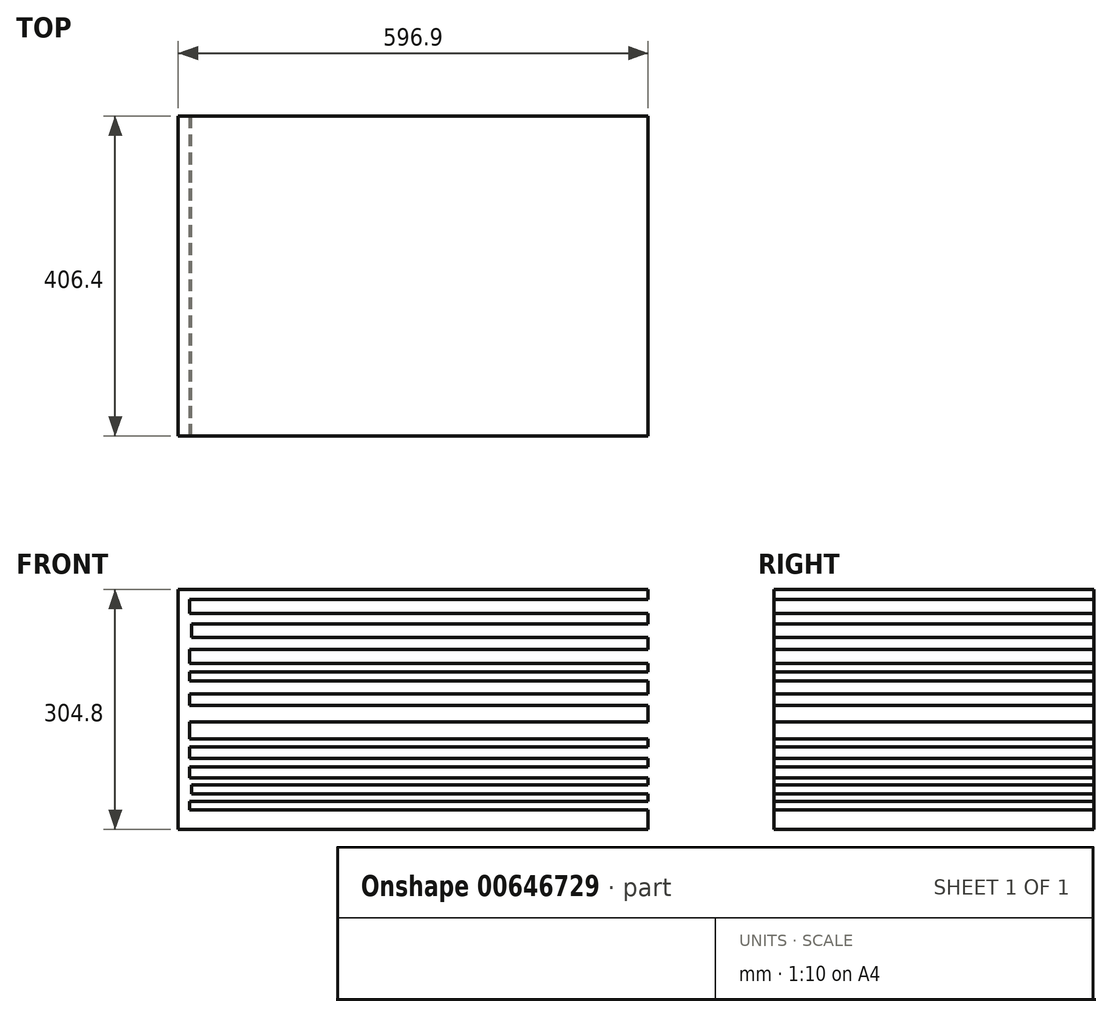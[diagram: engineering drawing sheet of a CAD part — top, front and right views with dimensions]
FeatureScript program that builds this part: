
annotation { "Feature Type Name" : "Feature", "Feature Type Description" : "" }
export const myFeature = defineFeature(function(context is Context, id is Id, definition is map)
    precondition{}
    {
        {
            var Q0;
            Q0=qCreatedBy(makeId("Front.planeOp"),FACE);
            var sketch = newSketch(context, id + "F0", { "sketchPlane" : qUnion([Q0])});
            skLineSegment(sketch, "E0.bottom", {"start": v(-41.59, 248.25) * mm, "end": v(555.31, 248.25) * mm});
            skLineSegment(sketch, "E0.top", {"start": v(-41.59, -56.55) * mm, "end": v(555.31, -56.55) * mm});
            skLineSegment(sketch, "E0.left", {"start": v(-41.59, 248.25) * mm, "end": v(-41.59, -56.55) * mm});
            skLineSegment(sketch, "E0.right", {"start": v(555.31, 248.25) * mm, "end": v(555.31, -56.55) * mm});
            skLineSegment(sketch, "E1.bottom", {"start": v(-26.88, 235.82) * mm, "end": v(557.3, 235.82) * mm});
            skLineSegment(sketch, "E1.top", {"start": v(-26.88, 217.95) * mm, "end": v(557.3, 217.95) * mm});
            skLineSegment(sketch, "E1.left", {"start": v(-26.88, 235.82) * mm, "end": v(-26.88, 217.95) * mm});
            skLineSegment(sketch, "E1.right", {"start": v(557.3, 235.82) * mm, "end": v(557.3, 217.95) * mm});
            skLineSegment(sketch, "E2.bottom", {"start": v(-24.73, 204.36) * mm, "end": v(557.3, 204.36) * mm});
            skLineSegment(sketch, "E2.top", {"start": v(-24.73, 187.2) * mm, "end": v(557.3, 187.2) * mm});
            skLineSegment(sketch, "E2.left", {"start": v(-24.73, 204.36) * mm, "end": v(-24.73, 187.2) * mm});
            skLineSegment(sketch, "E2.right", {"start": v(557.3, 204.36) * mm, "end": v(557.3, 187.2) * mm});
            skLineSegment(sketch, "E3.bottom", {"start": v(-26.88, 172.18) * mm, "end": v(557.3, 172.18) * mm});
            skLineSegment(sketch, "E3.top", {"start": v(-26.88, 154.3) * mm, "end": v(557.3, 154.3) * mm});
            skLineSegment(sketch, "E3.left", {"start": v(-26.88, 172.18) * mm, "end": v(-26.88, 154.3) * mm});
            skLineSegment(sketch, "E3.right", {"start": v(557.3, 172.18) * mm, "end": v(557.3, 154.3) * mm});
            skLineSegment(sketch, "E4.bottom", {"start": v(-26.88, 132.14) * mm, "end": v(557.3, 132.14) * mm});
            skLineSegment(sketch, "E4.top", {"start": v(-26.88, 143.58) * mm, "end": v(557.3, 143.58) * mm});
            skLineSegment(sketch, "E4.left", {"start": v(-26.88, 132.14) * mm, "end": v(-26.88, 143.58) * mm});
            skLineSegment(sketch, "E4.right", {"start": v(557.3, 132.14) * mm, "end": v(557.3, 143.58) * mm});
            skLineSegment(sketch, "E5.bottom", {"start": v(-26.88, 115.7) * mm, "end": v(557.3, 115.7) * mm});
            skLineSegment(sketch, "E5.top", {"start": v(-26.88, 100.68) * mm, "end": v(557.3, 100.68) * mm});
            skLineSegment(sketch, "E5.left", {"start": v(-26.88, 115.7) * mm, "end": v(-26.88, 100.68) * mm});
            skLineSegment(sketch, "E5.right", {"start": v(557.3, 115.7) * mm, "end": v(557.3, 100.68) * mm});
            skLineSegment(sketch, "E6.bottom", {"start": v(-26.88, 79.95) * mm, "end": v(557.3, 79.95) * mm});
            skLineSegment(sketch, "E6.top", {"start": v(-26.88, 58.5) * mm, "end": v(557.3, 58.5) * mm});
            skLineSegment(sketch, "E6.left", {"start": v(-26.88, 79.95) * mm, "end": v(-26.88, 58.5) * mm});
            skLineSegment(sketch, "E6.right", {"start": v(557.3, 79.95) * mm, "end": v(557.3, 58.5) * mm});
            skLineSegment(sketch, "E7.bottom", {"start": v(-26.88, 48.48) * mm, "end": v(557.3, 48.48) * mm});
            skLineSegment(sketch, "E7.top", {"start": v(-26.88, 33.47) * mm, "end": v(557.3, 33.47) * mm});
            skLineSegment(sketch, "E7.left", {"start": v(-26.88, 48.48) * mm, "end": v(-26.88, 33.47) * mm});
            skLineSegment(sketch, "E7.right", {"start": v(557.3, 48.48) * mm, "end": v(557.3, 33.47) * mm});
            skLineSegment(sketch, "E8.bottom", {"start": v(-26.88, 22.74) * mm, "end": v(557.3, 22.74) * mm});
            skLineSegment(sketch, "E8.top", {"start": v(-26.88, 9.16) * mm, "end": v(557.3, 9.16) * mm});
            skLineSegment(sketch, "E8.left", {"start": v(-26.88, 22.74) * mm, "end": v(-26.88, 9.16) * mm});
            skLineSegment(sketch, "E8.right", {"start": v(557.3, 22.74) * mm, "end": v(557.3, 9.16) * mm});
            skLineSegment(sketch, "E9.bottom", {"start": v(-24.73, 0) * mm, "end": v(557.3, 0) * mm});
            skLineSegment(sketch, "E9.top", {"start": v(-24.73, -11.58) * mm, "end": v(557.3, -11.58) * mm});
            skLineSegment(sketch, "E9.left", {"start": v(-24.73, 0) * mm, "end": v(-24.73, -11.58) * mm});
            skLineSegment(sketch, "E9.right", {"start": v(557.3, 0) * mm, "end": v(557.3, -11.58) * mm});
            skLineSegment(sketch, "E10.bottom", {"start": v(-26.88, -20.87) * mm, "end": v(557.3, -20.87) * mm});
            skLineSegment(sketch, "E10.top", {"start": v(-26.88, -31.6) * mm, "end": v(557.3, -31.6) * mm});
            skLineSegment(sketch, "E10.left", {"start": v(-26.88, -20.87) * mm, "end": v(-26.88, -31.6) * mm});
            skLineSegment(sketch, "E10.right", {"start": v(557.3, -20.87) * mm, "end": v(557.3, -31.6) * mm});
            skSolve(sketch);
        }
        {
            var Q0;
            Q0=makeQuery(id+"F0.imprint","IMPRINT",FACE,{"disambiguationData":[TD([[makeQuery(id+"F0.imprint","IMPRINT",EDGE,{"derivedFrom":sQuery(id+"F0.wireOp",EDGE,"E0.bottom")}),-1.0]])]});
            extrude(context, id + "F1", {"entities" : qUnion([Q0]), "depth" : 406.4 * mm, "offsetDistance" : 25.4 * mm});
        }
    });
